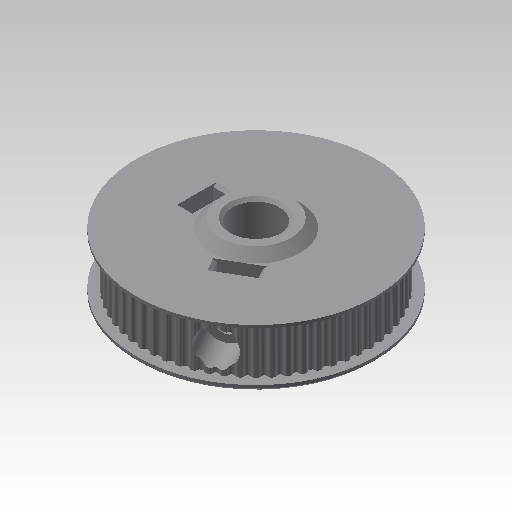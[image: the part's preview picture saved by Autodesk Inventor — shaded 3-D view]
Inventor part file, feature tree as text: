
AUTODESK INVENTOR PART (.ipt)
format: ipt  version: 2020 (Build 240168000, 168)  size: 675,840 bytes
history: native  units: mm
features: sketch x4, extrude x3, revolve x2, pattern_circular x2, plane x2, chamfer x2, fillet x1
ambient origin geometry x8: Origin, YZ Plane, XZ Plane, XY Plane, X Axis, Y Axis, Z Axis, Center Point
bodies: Solid1 (feature_tree)
feature tree (16):
  revolve  "Revolution1"  [1 undecoded]
  extrude  "Extrusion1"  Depth=10.0mm TaperAngle=360.0deg
  fillet  "Fillet1"  Radius=18.85mm
  pattern_circular  "Circular Pattern1"  [2 undecoded]
  sketch  "Sketch3"  dims[d10=10.0mm d11=0.0mm d12=600.0mm d13=360.0deg d18=18.85mm]
  revolve  "Revolution2"  [1 undecoded]
  plane  "Work Plane1"
  extrude  "Extrusion2"  Depth=4.0mm
  chamfer  "Chamfer1"  Angle=120.0deg  [1 undecoded]
  plane  "Work Plane2"
  extrude  "Extrusion3"  Depth=4.0mm
  pattern_circular  "Circular Pattern2"  [2 undecoded]
  chamfer  "Chamfer2"  Distance=1.7mm
  sketch  "Sketch2"  dims[d7=90.0deg d8=1.1mm]
  sketch  "Sketch4"  dims[d19=0.3mm]
  sketch  "Sketch5"  dims[d20=7.5mm d21=1.0mm d22=1.5mm d23=0.5mm d24=120.0deg d25=4.0mm d26=18.85mm d27=1.7mm d28=1.7mm d29=90.0deg d31=-7.5mm d32=5.7mm d33=5.7mm d34=2.6mm d35=0.0mm d36=5.0mm d37=0.5mm d38=2.0mm d39=45.0deg d40=20.0mm d41=120.0deg d43=0.5mm d44=2.0mm d45=45.0deg d46=1.5mm d47=2.0mm d48=135.0deg d49=-3.0mm d50=6.0mm d51=30.71mm d52=0.0mm]
note: 7 required parameter values undecoded (feature->parameter linkage not recoverable at this tier; creation-order binding heuristic only, values carry confidence <= 0.55)